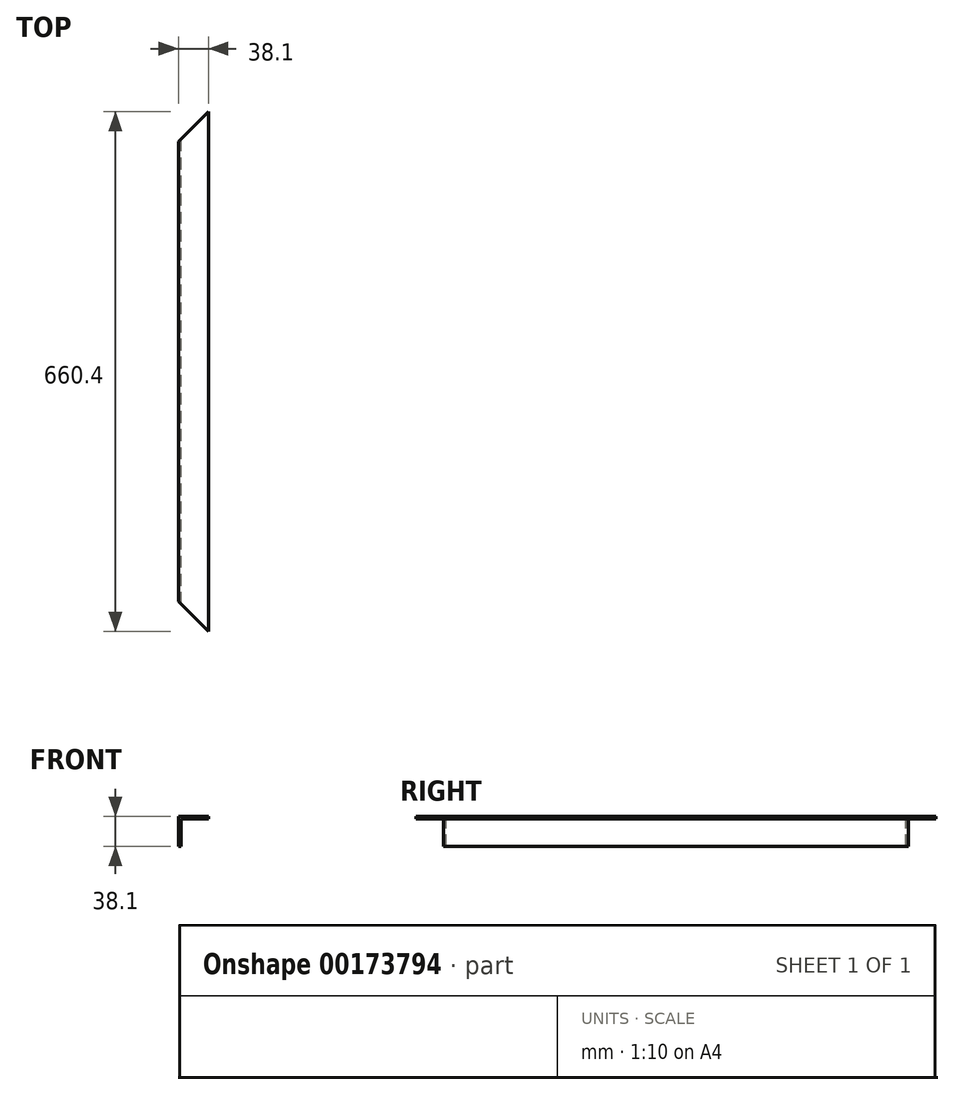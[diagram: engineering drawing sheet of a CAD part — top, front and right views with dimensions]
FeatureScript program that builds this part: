
annotation { "Feature Type Name" : "Feature", "Feature Type Description" : "" }
export const myFeature = defineFeature(function(context is Context, id is Id, definition is map)
    precondition{}
    {
        {
            var Q0;
            Q0=qCreatedBy(makeId("Front.planeOp"),FACE);
            var sketch = newSketch(context, id + "F0", { "sketchPlane" : qUnion([Q0])});
            skLineSegment(sketch, "E0.bottom", {"start": v(19.05, 19.05) * mm, "end": v(-19.05, 19.05) * mm});
            skLineSegment(sketch, "E0.top", {"start": v(-15.88, -19.05) * mm, "end": v(-19.05, -19.05) * mm});
            skLineSegment(sketch, "E0.left", {"start": v(19.05, 19.05) * mm, "end": v(19.05, 15.88) * mm});
            skLineSegment(sketch, "E0.right", {"start": v(-19.05, 19.05) * mm, "end": v(-19.05, -19.05) * mm});
            skPoint(sketch, "E0.middle", {"position": v(0, 0) * mm});
            skLineSegment(sketch, "E1", {"start": v(19.05, 15.88) * mm, "end": v(-15.88, 15.88) * mm});
            skLineSegment(sketch, "E2", {"start": v(-15.88, 15.88) * mm, "end": v(-15.88, -19.05) * mm});
            skPoint(sketch, "E3.orphan", {"position": v(19.05, -19.05) * mm});
            skSolve(sketch);
        }
        {
            var Q0;
            Q0=makeQuery(id+"F0.imprint","IMPRINT",FACE,{"disambiguationData":[TD([[makeQuery(id+"F0.imprint","IMPRINT",EDGE,{"derivedFrom":sQuery(id+"F0.wireOp",EDGE,"E0.bottom")}),1.0]])]});
            extrude(context, id + "F1", {"entities" : qUnion([Q0]), "depth" : 660.4 * mm});
        }
        {
            var Q0;
            Q0=makeQuery(id+"F1.opExtrude","SWEPT_FACE",FACE,{"disambiguationData":[OSD([sQuery(id+"F0.wireOp",EDGE,"E0.bottom")])]});
            var sketch = newSketch(context, id + "F2", { "sketchPlane" : qUnion([Q0])});
            skLineSegment(sketch, "E4", {"start": v(19.05, -660.4) * mm, "end": v(-19.05, -622.3) * mm});
            skLineSegment(sketch, "E5.0", {"start": v(-19.05, -660.4) * mm, "end": v(-19.05, -622.3) * mm});
            skLineSegment(sketch, "E6.0", {"start": v(19.05, -660.4) * mm, "end": v(-19.05, -660.4) * mm});
            skPoint(sketch, "E7.orphan", {"position": v(-19.05, 0) * mm});
            skLineSegment(sketch, "E8.filletArc", {"start": v(-19.05, -622.3) * mm, "end": v(-19.05, -622.3) * mm});
            skLineSegment(sketch, "E9", {"start": v(19.05, 0) * mm, "end": v(-19.05, -38.1) * mm});
            skPoint(sketch, "E10.0", {"position": v(0, 0) * mm});
            skLineSegment(sketch, "E11.trimOffspring", {"start": v(-19.05, -38.1) * mm, "end": v(-19.05, 0) * mm});
            skLineSegment(sketch, "E12.filletArc", {"start": v(-19.05, -38.1) * mm, "end": v(-19.05, -38.1) * mm});
            skSolve(sketch);
        }
        {
            var Q0;
            Q0 = qSketchRegion(id + "F2", true);
            var Q1;
            Q1=makeQuery(id+"F2.imprint","IMPRINT",FACE,{"disambiguationData":[TD([[makeQuery(id+"F2.imprint","IMPRINT",EDGE,{"derivedFrom":sQuery(id+"F2.wireOp",EDGE,"E9")}),-1.0]])]});
            extrude(context, id + "F3", {"entities" : qUnion([Q0, Q1]), "operationType" : NewBodyOperationType.REMOVE, "endBound" : BoundingType.THROUGH_ALL, "oppositeDirection" : true, "depth" : 25.4 * mm});
        }
    });
